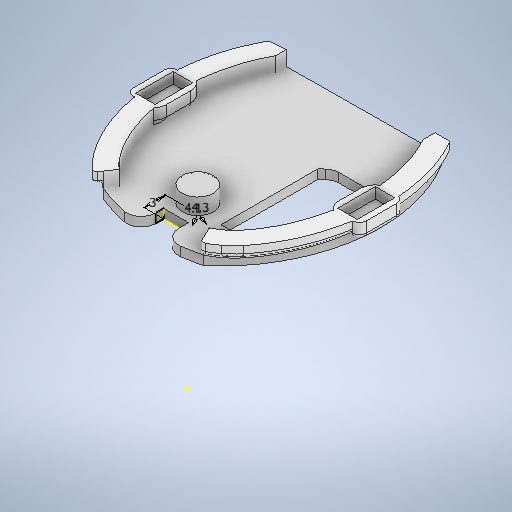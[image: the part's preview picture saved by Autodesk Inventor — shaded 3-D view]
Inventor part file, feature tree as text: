
AUTODESK INVENTOR PART (.ipt)
format: ipt  version: 2025.4 (Build 294407000, 407)  size: 704,000 bytes
history: native  units: in
note: dims shown in document units (in); Inventor stores cm internally (conversion verified against a paired STEP export)
features: sketch x10, fillet x9, extrude x8, other x3
ambient origin geometry x8: Origin, YZ Plane, XZ Plane, XY Plane, X Axis, Y Axis, Z Axis, Center Point
bodies: Solid1 (feature_tree), Solid2 (feature_tree)
feature tree (30):
  other  "rat_cap_EC_v12.iam"
  other  "rat_cap_walls_v8.iam:1::rat_cap_left_wall_v8.ipt:1"
  other  "rat_cap_walls_v8.iam:1::rat_cap_right_wall_v8.ipt:1"
  extrude  "Extrusion1"  Depth=0.3937in TaperAngle=0.0deg
  sketch  "Sketch3"  dims[d16=0.315in d17=0.0812in d18=0.0in]
  extrude  "Extrusion4"  Depth=0.0812in TaperAngle=0.0deg
  extrude  "Extrusion5"  Depth=0.0787in
  fillet  "Fillet5"  Radius=0.0787in
  fillet  "Fillet6"  Radius=0.0787in
  fillet  "Fillet7"  Radius=0.0787in
  fillet  "Fillet8"  Radius=0.0787in
  fillet  "Fillet10"  Radius=0.0787in
  fillet  "Fillet11"  Radius=0.0394in
  fillet  "Fillet12"  Radius=0.0787in
  sketch  "Sketch17"  dims[d79=0.05in d80=0.0in d81=0.1181in]
  extrude  "Extrusion16"  Depth=0.0394in
  fillet  "Fillet17"  Radius=0.0394in
  fillet  "Fillet18"  Radius=0.0197in
  extrude  "Extrusion17"  Depth=0.1181in
  extrude  "Extrusion19"  Depth=0.1378in TaperAngle=0.0deg
  sketch  "Sketch23"  dims[d35=0.0197in]
  extrude  "Extrusion20"  Depth=0.1339in TaperAngle=0.0deg
  sketch  "Sketch24"  dims[d36=0.0344in d58=0.0197in d59=0.0344in d60=0.0197in d61=0.0344in d75=0.0197in d76=0.0344in d77=0.0197in d78=0.0344in d88=0.0197in d89=0.0344in]
  extrude  "Extrusion21"  Depth=0.0344in
  sketch  "Sketch1"  dims[d0=0.3937in d1=0.05in d2=0.0in]
  sketch  "Sketch5"  dims[d19=0.0812in d20=0.0in d42=0.0787in d43=0.0787in d48=0.0787in d49=0.0787in d51=0.0787in d52=0.0787in d53=0.0394in d64=0.0787in]
  sketch  "Sketch6"  dims[d65=0.3878in d66=0.0in d67=0.0394in d68=0.0394in d72=0.0197in d73=0.0in]
  sketch  "Sketch18"  dims[d82=0.1693in d83=0.1378in d84=0.0in]
  sketch  "Sketch19"  dims[d85=0.1614in d86=0.1339in d87=0.0in]
  sketch  "Sketch22"  dims[d33=0.0197in d34=0.0344in]
